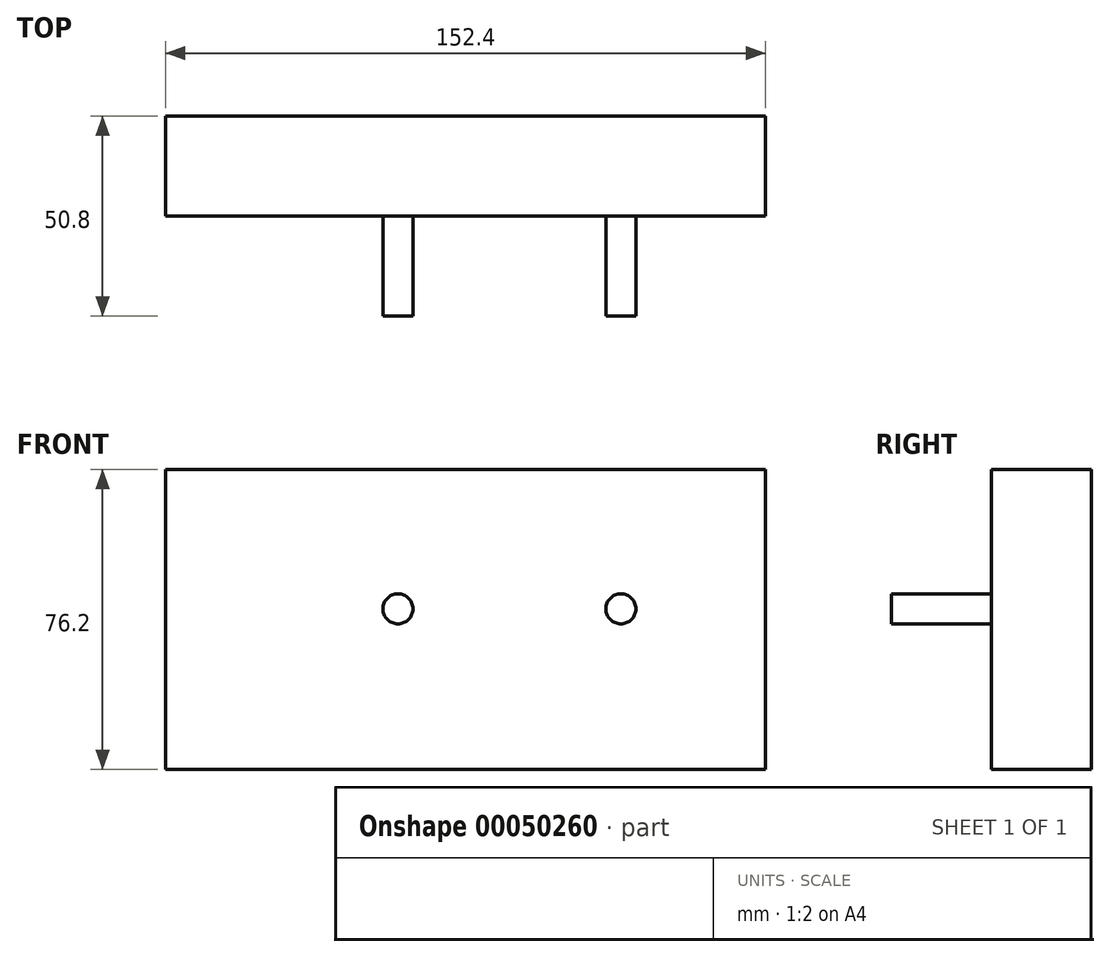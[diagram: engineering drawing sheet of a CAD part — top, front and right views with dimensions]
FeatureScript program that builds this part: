
annotation { "Feature Type Name" : "Feature", "Feature Type Description" : "" }
export const myFeature = defineFeature(function(context is Context, id is Id, definition is map)
    precondition{}
    {
        {
            var Q0;
            Q0=qCreatedBy(makeId("Front.planeOp"),FACE);
            var sketch = newSketch(context, id + "F0", { "sketchPlane" : qUnion([Q0])});
            skLineSegment(sketch, "E0", {"start": v(0, 0) * mm, "end": v(152.4, 0) * mm});
            skLineSegment(sketch, "E1", {"start": v(152.4, 0) * mm, "end": v(152.4, 76.2) * mm});
            skLineSegment(sketch, "E2", {"start": v(152.4, 76.2) * mm, "end": v(0, 76.2) * mm});
            skLineSegment(sketch, "E3", {"start": v(0, 76.2) * mm, "end": v(0, 0) * mm});
            skSolve(sketch);
        }
        {
            var Q0;
            Q0 = qSketchRegion(id + "F0", true);
            extrude(context, id + "F1", {"entities" : qUnion([Q0]), "depth" : 25.4 * mm});
        }
        {
            var Q0;
            Q0=makeQuery(id+"F1.opExtrude","CAP_FACE",FACE,{"disambiguationData":[OSD([sQuery(id+"F0.wireOp",EDGE,"E0"),sQuery(id+"F0.wireOp",EDGE,"E1"),sQuery(id+"F0.wireOp",EDGE,"E2"),sQuery(id+"F0.wireOp",EDGE,"E3")])],"isStart":false});
            var sketch = newSketch(context, id + "F2", { "sketchPlane" : qUnion([Q0])});
            skCircle(sketch, "E4", {"center": v(59.02, 40.8) * mm, "radius": 3.81 * mm});
            skLineSegment(sketch, "E5", {"start": v(59.02, 40.8) * mm, "end": v(115.66, 40.8) * mm});
            skCircle(sketch, "E6", {"center": v(115.66, 40.8) * mm, "radius": 3.81 * mm});
            skSolve(sketch);
        }
        {
            var Q0;
            Q0 = qSketchRegion(id + "F2", true);
            extrude(context, id + "F3", {"entities" : qUnion([Q0]), "operationType" : NewBodyOperationType.ADD, "depth" : 25.4 * mm});
        }
    });
